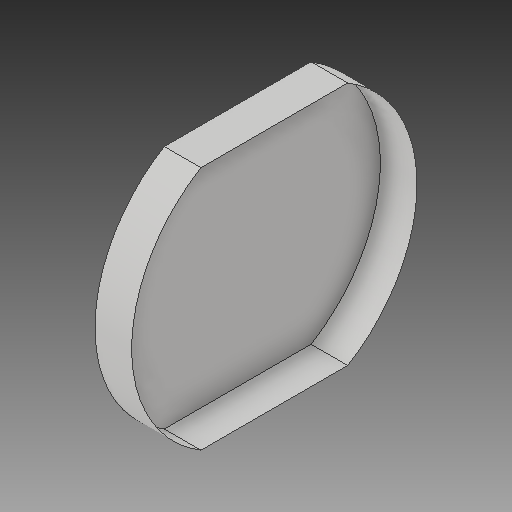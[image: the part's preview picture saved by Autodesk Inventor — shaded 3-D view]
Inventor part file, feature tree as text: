
AUTODESK INVENTOR PART (.ipt)
format: ipt  version: 2017 (Build 210142000, 142)  size: 117,248 bytes
history: native  units: in
note: dims shown in document units (in); Inventor stores cm internally (conversion verified against a paired STEP export)
features: extrude x1, delete_face x1, sketch x1
ambient origin geometry x8: Origin, YZ Plane, XZ Plane, XY Plane, X Axis, Y Axis, Z Axis, Center Point
bodies: Solid2 (feature_tree)
feature tree (3):
  extrude  "connection"  [1 undecoded]
  delete_face  "Delete Face1"
  sketch  "Sketch1"  dims[d12=6.6667in d14=1.0in d15=0.0in d85=4.0in d87=3.8873in d88=3.8873in d92=1.6458in d98=3.3333in]
note: 1 required parameter value undecoded (feature->parameter linkage not recoverable at this tier; creation-order binding heuristic only, values carry confidence <= 0.55)
